# Revit family: 304_Cim3790-_
name_source: partatom
category: Pipe Accessories
units: mm (PartAtom-declared; Revit-internal decimal feet)

## family parameters
Always vertical = Yes
Cut with Voids When Loaded = No
Part Type = Valve - Breaks Into
Round Connector Dimension = Use Diameter
Shared = No
Work Plane-Based = No

## types (15) — shared parameters
B1 = 7 mm  [stored 0.0229659 ft]
CAT0 = Yes
DD1 = 15 mm  [stored 0.0492126 ft]
Description = AUTOMATIC BALANCING VALVE - PN 16 - FLANGED END
L = 170 mm  [stored 0.557743 ft]
L2D = 170 mm  [stored 0.557743 ft]
L2D_Min = 3048 mm
LL1 = 85 mm  [stored 0.278871 ft]
LL2 = 80 mm  [stored 0.262467 ft]
LL3 = 43 mm
Manufacturer = Cimberio
QmdConnectorList = 301;D;302;D
URL = www.cimberio.it
WW1 = 10 mm  [stored 0.0328084 ft]
magiPartTypeId = 304
magiProductFamilyId = Cim3790-*
zero-valued in all types: MC_Default_elevation

## per-type parameters (varying)
| type | A | D | HH1 | HH2 | W2D |
| Cim3790-50 | 100 mm  [stored 0.328084 ft] | 50 mm | 50 mm  [stored 0.164042 ft] | 111 mm | 50 mm  [stored 0.164042 ft] |
| Cim3790-800 | 880 mm | 800 mm | 440 mm | 111 mm | 800 mm |
| Cim3790-600 | 715 mm | 600 mm | 358 mm | 111 mm | 600 mm |
| Cim3790-500 | 601 mm | 500 mm | 301 mm | 111 mm | 500 mm |
| Cim3790-450 | 545 mm | 450 mm | 273 mm | 111 mm | 450 mm |
| Cim3790-400 | 496 mm | 400 mm | 248 mm  [stored 0.813648 ft] | 111 mm | 400 mm  [stored 1.31234 ft] |
| Cim3790-350 | 443 mm | 350 mm | 222 mm | 111 mm | 350 mm  [stored 1.14829 ft] |
| Cim3790-300 | 383 mm  [stored 1.25656 ft] | 300 mm | 192 mm | 111 mm | 300 mm  [stored 0.984252 ft] |
| Cim3790-250 | 326 mm  [stored 1.06955 ft] | 250 mm | 163 mm  [stored 0.534777 ft] | 107 mm | 250 mm  [stored 0.82021 ft] |
| Cim3790-200 | 271 mm  [stored 0.889108 ft] | 200 mm | 136 mm | 111 mm | 200 mm  [stored 0.656168 ft] |
| Cim3790-150 | 216 mm  [stored 0.708661 ft] | 150 mm | 108 mm  [stored 0.354331 ft] | 111 mm | 150 mm  [stored 0.492126 ft] |
| Cim3790-125 | 193 mm  [stored 0.633202 ft] | 125 mm | 97 mm | 111 mm | 125 mm  [stored 0.410105 ft] |
| Cim3790-100 | 163 mm  [stored 0.534777 ft] | 100 mm | 82 mm | 111 mm | 100 mm  [stored 0.328084 ft] |
| Cim3790-80 | 131 mm  [stored 0.42979 ft] | 80 mm | 66 mm | 111 mm | 80 mm  [stored 0.262467 ft] |
| Cim3790-65 | 119 mm  [stored 0.39042 ft] | 65 mm | 60 mm | 111 mm | 65 mm  [stored 0.213255 ft] |

note: column(s) folded — value = type name in every type: magiProductCode, magiProductId

note: [stored X ft] marks values corroborated as IEEE doubles in the binary element streams (Revit-internal decimal feet)

## geometry (parser evidence)
native form markers: Sweep x1
no freeform markers — native parametric forms only
